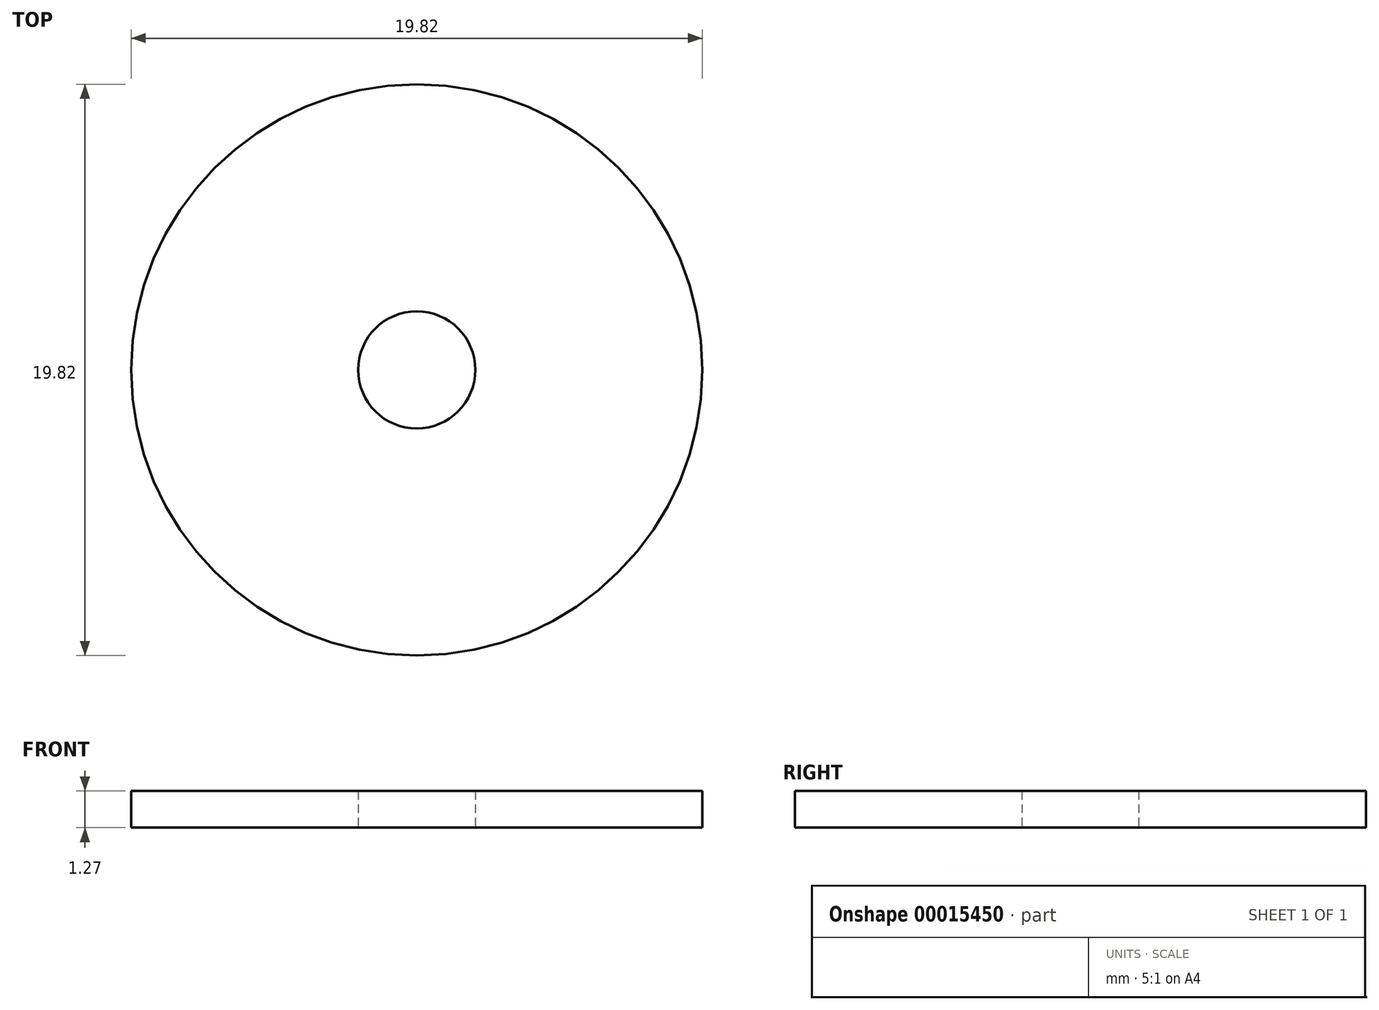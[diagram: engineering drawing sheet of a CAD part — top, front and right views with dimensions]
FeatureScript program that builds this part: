
annotation { "Feature Type Name" : "Feature", "Feature Type Description" : "" }
export const myFeature = defineFeature(function(context is Context, id is Id, definition is map)
    precondition{}
    {
        {
            var Q0;
            Q0=qCreatedBy(makeId("Top.planeOp"),FACE);
            var sketch = newSketch(context, id + "F0", { "sketchPlane" : qUnion([Q0])});
            skCircle(sketch, "E0", {"center": v(0, 0) * mm, "radius": 9.9 * mm});
            skCircle(sketch, "E1", {"center": v(0, 0) * mm, "radius": 2.03 * mm});
            skSolve(sketch);
        }
        {
            var Q0;
            Q0 = qSketchRegion(id + "F0", true);
            extrude(context, id + "F1", {"entities" : qUnion([Q0]), "depth" : 1.27 * mm});
        }
    });
